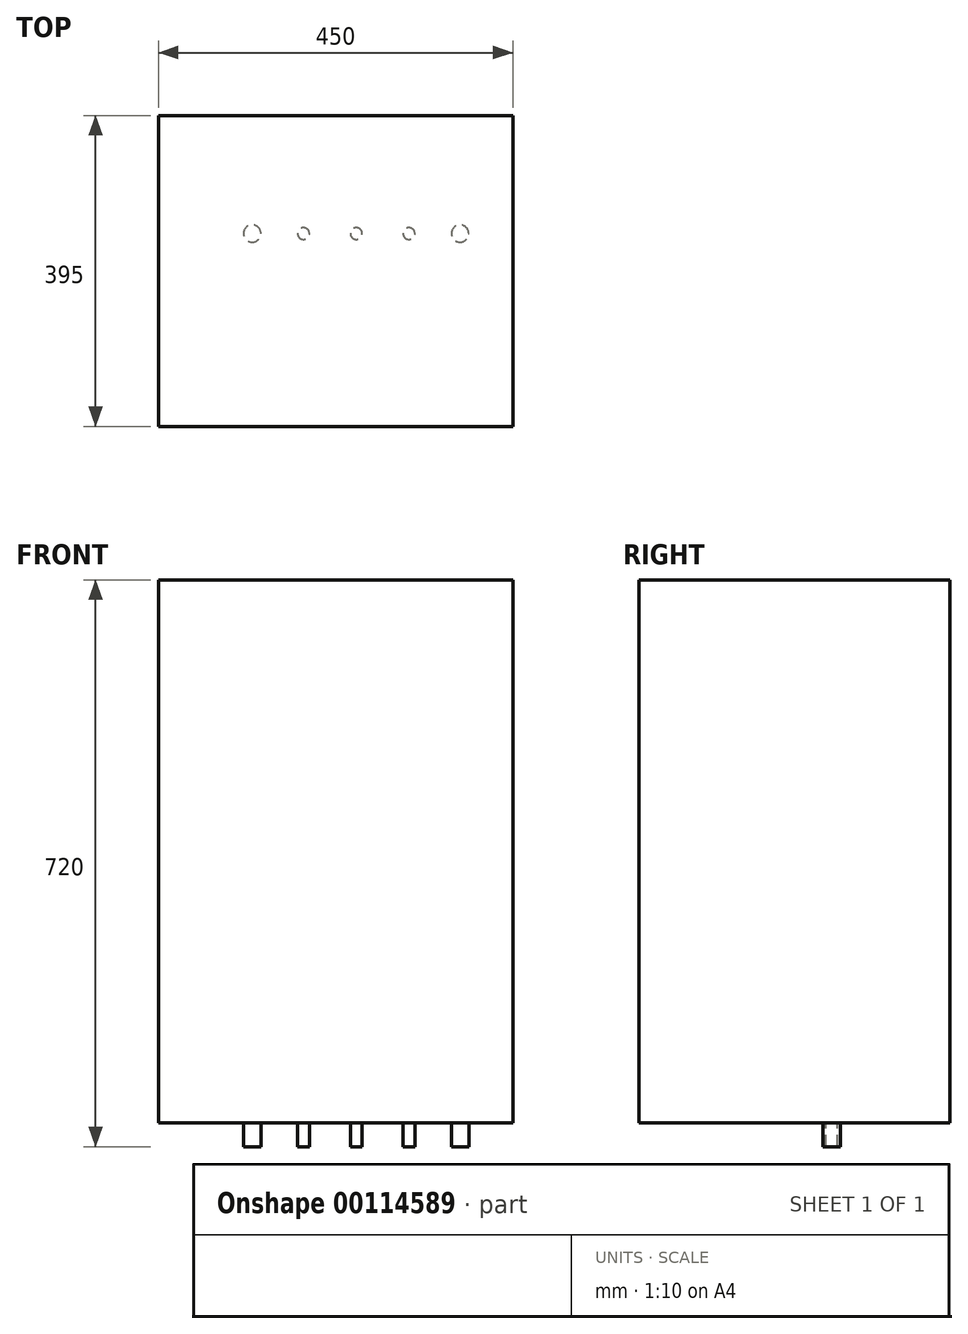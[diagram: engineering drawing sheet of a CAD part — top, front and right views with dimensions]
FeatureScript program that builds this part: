
annotation { "Feature Type Name" : "Feature", "Feature Type Description" : "" }
export const myFeature = defineFeature(function(context is Context, id is Id, definition is map)
    precondition{}
    {
        {
            var Q0;
            Q0=qCreatedBy(makeId("Top.planeOp"),FACE);
            var sketch = newSketch(context, id + "F0", { "sketchPlane" : qUnion([Q0])});
            skLineSegment(sketch, "E0.bottom", {"start": v(-198.76, 286.42) * mm, "end": v(251.24, 286.42) * mm});
            skLineSegment(sketch, "E0.top", {"start": v(-198.76, -108.58) * mm, "end": v(251.24, -108.58) * mm});
            skLineSegment(sketch, "E0.left", {"start": v(-198.76, 286.42) * mm, "end": v(-198.76, -108.58) * mm});
            skLineSegment(sketch, "E0.right", {"start": v(251.24, 286.42) * mm, "end": v(251.24, -108.58) * mm});
            skLineSegment(sketch, "E1", {"start": v(26.24, -108.58) * mm, "end": v(26.24, 286.42) * mm, "construction": true});
            skSolve(sketch);
        }
        {
            var Q0;
            Q0 = qSketchRegion(id + "F0", true);
            extrude(context, id + "F1", {"entities" : qUnion([Q0]), "depth" : 690 * mm, "offsetDistance" : 25 * mm});
        }
        {
            var Q0;
            Q0=makeQuery(id+"F0.imprint","IMPRINT",FACE,{"disambiguationData":[TD([[makeQuery(id+"F0.imprint","IMPRINT",EDGE,{"derivedFrom":sQuery(id+"F0.wireOp",EDGE,"E0.bottom")}),-1.0]])]});
            var sketch = newSketch(context, id + "F2", { "sketchPlane" : qUnion([Q0])});
            skLineSegment(sketch, "E2", {"start": v(-198.76, 136.42) * mm, "end": v(251.24, 136.42) * mm, "construction": true});
            skCircle(sketch, "E3", {"center": v(184.24, 136.42) * mm, "radius": 11 * mm});
            skCircle(sketch, "E4", {"center": v(119.24, 136.42) * mm, "radius": 7.5 * mm});
            skCircle(sketch, "E5", {"center": v(52.24, 136.42) * mm, "radius": 7.5 * mm});
            skCircle(sketch, "E6", {"center": v(-14.76, 136.42) * mm, "radius": 7.5 * mm});
            skCircle(sketch, "E7", {"center": v(-79.76, 136.42) * mm, "radius": 11 * mm});
            skSolve(sketch);
        }
        {
            var Q0;
            Q0 = qSketchRegion(id + "F2", true);
            extrude(context, id + "F3", {"entities" : qUnion([Q0]), "operationType" : NewBodyOperationType.ADD, "oppositeDirection" : true, "depth" : 30 * mm, "offsetDistance" : 25 * mm});
        }
    });
